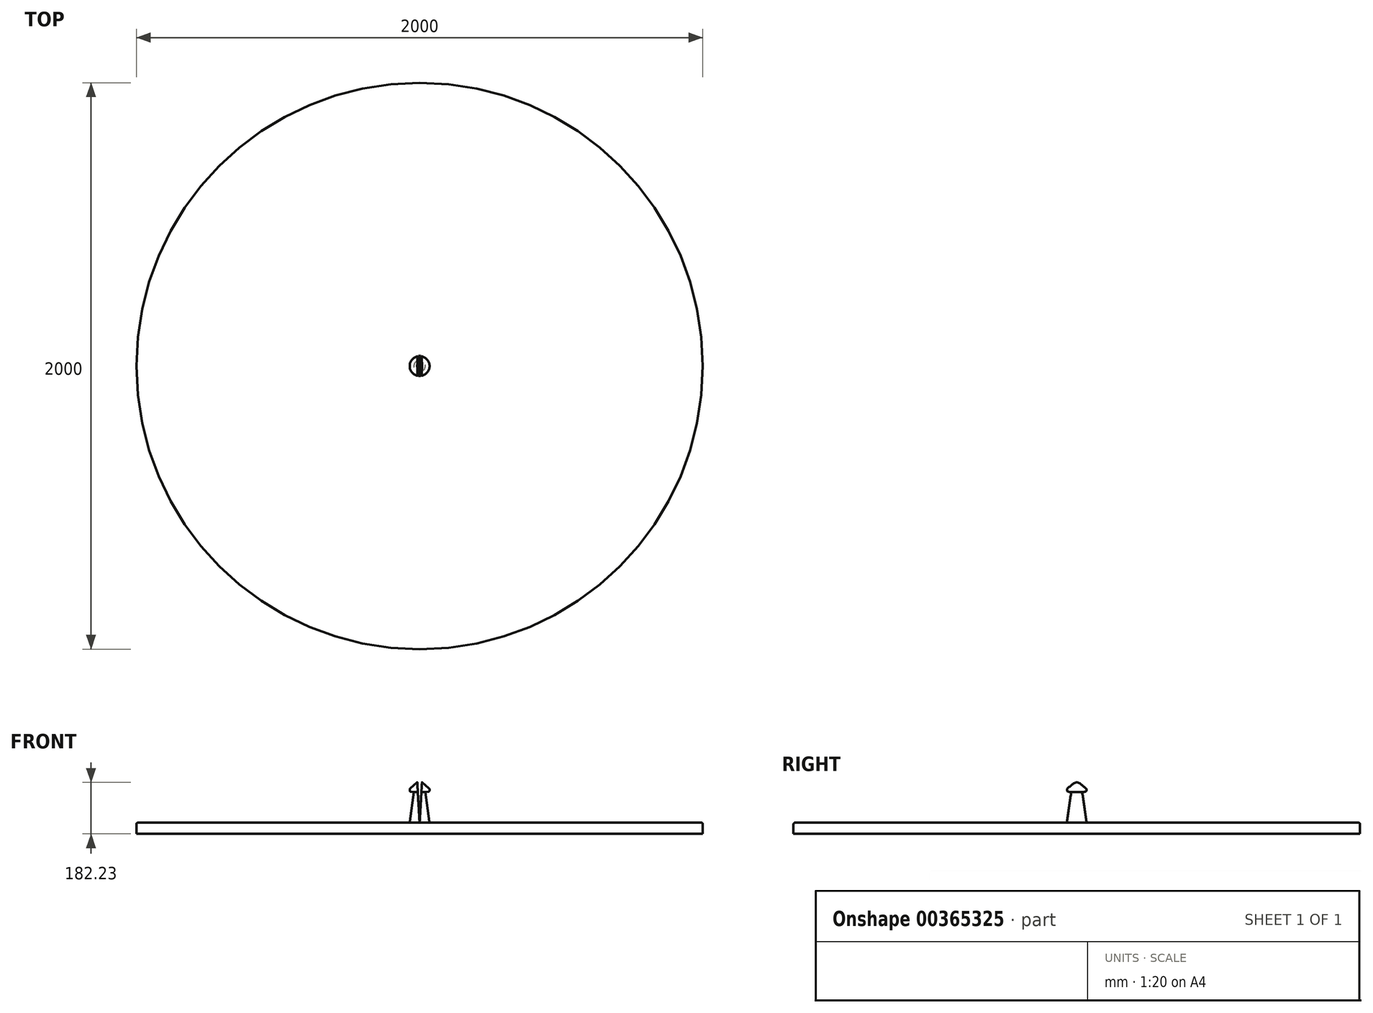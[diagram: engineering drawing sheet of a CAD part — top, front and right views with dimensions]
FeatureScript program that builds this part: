
annotation { "Feature Type Name" : "Feature", "Feature Type Description" : "" }
export const myFeature = defineFeature(function(context is Context, id is Id, definition is map)
    precondition{}
    {
        {
            var Q0;
            Q0=qCreatedBy(makeId("Front.planeOp"),FACE);
            var sketch = newSketch(context, id + "F0", { "sketchPlane" : qUnion([Q0])});
            skLineSegment(sketch, "E0.bottom", {"start": v(0, 0) * mm, "end": v(1000, 0) * mm});
            skLineSegment(sketch, "E0.top", {"start": v(0, -39.44) * mm, "end": v(1000, -39.44) * mm});
            skLineSegment(sketch, "E0.right", {"start": v(1000, 0) * mm, "end": v(1000, -39.44) * mm});
            skLineSegment(sketch, "E1", {"start": v(35, 0) * mm, "end": v(20.14, 107.95) * mm});
            skLineSegment(sketch, "E2", {"start": v(20.14, 107.95) * mm, "end": v(35, 110) * mm});
            skLineSegment(sketch, "E3", {"start": v(35, 110) * mm, "end": v(35, 120) * mm});
            skLineSegment(sketch, "E4", {"start": v(35, 120) * mm, "end": v(0, 150) * mm});
            skLineSegment(sketch, "E5", {"start": v(0, 150) * mm, "end": v(0, 0) * mm});
            skLineSegment(sketch, "E6", {"start": v(0, 0) * mm, "end": v(0, -39.44) * mm});
            skPoint(sketch, "E7.MirrorCS.end.orphan", {"position": v(0, 150) * mm});
            skPoint(sketch, "E7.MirrorCS.start.orphan", {"position": v(-35, 120) * mm});
            skPoint(sketch, "E8.MirrorCS.start.orphan", {"position": v(-35, 110) * mm});
            skPoint(sketch, "E9.MirrorCS.start.orphan", {"position": v(-20.14, 107.95) * mm});
            skPoint(sketch, "E10.MirrorCS.start.orphan", {"position": v(-35, 0) * mm});
            skPoint(sketch, "E0.left.end.orphan", {"position": v(-1000, -39.44) * mm});
            skPoint(sketch, "E0.left.start.orphan", {"position": v(-1000, 0) * mm});
            skSolve(sketch);
        }
        {
            var Q0;
            Q0 = qSketchRegion(id + "F0", true);
            var Q1;
            Q1=sQuery(id+"F0.wireOp",EDGE,"E5");
            revolve(context, id + "F1", {"entities" : qUnion([Q0]), "axis" : qUnion([Q1]), "revolveType" : RevolveType.FULL});
        }
        {
            var Q0;
            Q0=qCreatedBy(makeId("Front.planeOp"),FACE);
            var sketch = newSketch(context, id + "F2", { "sketchPlane" : qUnion([Q0])});
            skLineSegment(sketch, "E11", {"start": v(0, 0) * mm, "end": v(9.26, 157.24) * mm});
            skLineSegment(sketch, "E12", {"start": v(9.26, 157.24) * mm, "end": v(0, 157.8) * mm});
            skLineSegment(sketch, "E13.MirrorCS", {"start": v(-9.26, 157.24) * mm, "end": v(0, 157.8) * mm});
            skLineSegment(sketch, "E14.MirrorCS", {"start": v(0, 0) * mm, "end": v(-9.26, 157.24) * mm});
            skSolve(sketch);
        }
        {
            var Q0;
            Q0 = qSketchRegion(id + "F2", true);
            extrude(context, id + "F3", {"entities" : qUnion([Q0]), "operationType" : NewBodyOperationType.REMOVE, "endBound" : BoundingType.THROUGH_ALL, "depth" : 100 * mm, "hasSecondDirection" : true, "secondDirectionBound" : SecondDirectionBoundingType.THROUGH_ALL, "secondDirectionOppositeDirection" : true, "secondDirectionDepth" : 25 * mm});
        }
        {
            var Q0;
            {var subQ0=sQuery(id+"F0.wireOp",EDGE,"E3");var subQ1=sQuery(id+"F0.wireOp",EDGE,"E4");Q0=makeQuery(id+"F3.boolean.opBoolean","SPLIT",EDGE,{"disambiguationData":[TD([makeQuery(id+"F3.opExtrude","SWEPT_FACE",FACE,{"disambiguationData":[OSD([sQuery(id+"F2.wireOp",EDGE,"E11")])]})])],"derivedFrom":makeQuery(id+"F1.opRevolve","SWEPT_EDGE",EDGE,{"disambiguationData":[OSD([subQ0,subQ1])]})});}
            var Q1;
            {var subQ0=sQuery(id+"F0.wireOp",EDGE,"E3");var subQ1=sQuery(id+"F0.wireOp",EDGE,"E4");Q1=makeQuery(id+"F3.boolean.opBoolean","SPLIT",EDGE,{"disambiguationData":[TD([makeQuery(id+"F3.opExtrude","SWEPT_FACE",FACE,{"disambiguationData":[OSD([sQuery(id+"F2.wireOp",EDGE,"E14.MirrorCS")])]})])],"derivedFrom":makeQuery(id+"F1.opRevolve","SWEPT_EDGE",EDGE,{"disambiguationData":[OSD([subQ0,subQ1])]})});}
            var Q2;
            {var subQ0=sQuery(id+"F0.wireOp",EDGE,"E2");var subQ1=sQuery(id+"F0.wireOp",EDGE,"E3");Q2=makeQuery(id+"F3.boolean.opBoolean","SPLIT",EDGE,{"disambiguationData":[TD([makeQuery(id+"F3.opExtrude","SWEPT_FACE",FACE,{"disambiguationData":[OSD([sQuery(id+"F2.wireOp",EDGE,"E14.MirrorCS")])]})])],"derivedFrom":makeQuery(id+"F1.opRevolve","SWEPT_EDGE",EDGE,{"disambiguationData":[OSD([subQ0,subQ1])]})});}
            var Q3;
            {var subQ0=sQuery(id+"F0.wireOp",EDGE,"E2");var subQ1=sQuery(id+"F0.wireOp",EDGE,"E3");Q3=makeQuery(id+"F3.boolean.opBoolean","SPLIT",EDGE,{"disambiguationData":[TD([makeQuery(id+"F3.opExtrude","SWEPT_FACE",FACE,{"disambiguationData":[OSD([sQuery(id+"F2.wireOp",EDGE,"E11")])]})])],"derivedFrom":makeQuery(id+"F1.opRevolve","SWEPT_EDGE",EDGE,{"disambiguationData":[OSD([subQ0,subQ1])]})});}
            var Q4;
            Q4=makeQuery(id+"F1.opRevolve","SWEPT_FACE",FACE,{"disambiguationData":[OSD([sQuery(id+"F0.wireOp",EDGE,"E0.bottom")])]});
            fillet(context, id + "F4", {"entities" : qUnion([Q0, Q1, Q2, Q3, Q4]), "radius" : 5 * mm, "tangentPropagation" : true, "allowEdgeOverflow" : false});
        }
    });
